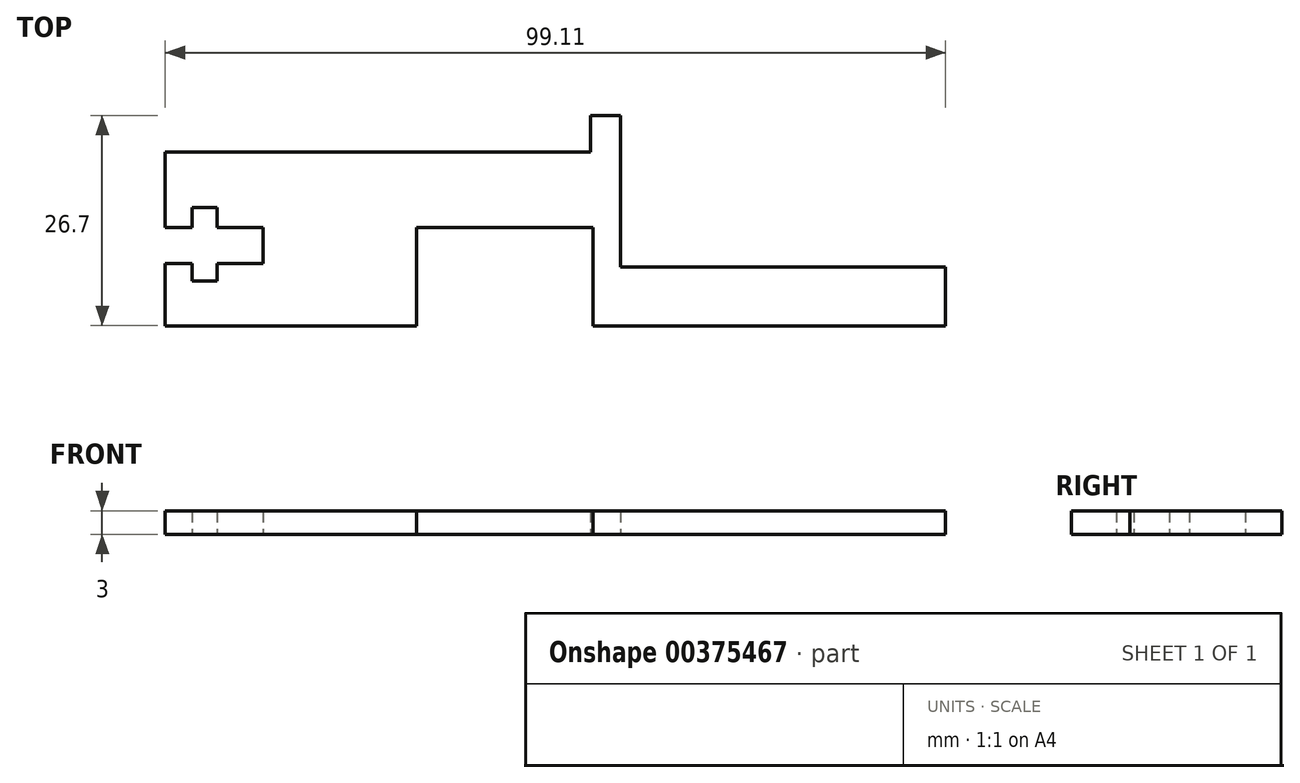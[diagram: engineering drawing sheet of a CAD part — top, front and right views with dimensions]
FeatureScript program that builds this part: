
annotation { "Feature Type Name" : "Feature", "Feature Type Description" : "" }
export const myFeature = defineFeature(function(context is Context, id is Id, definition is map)
    precondition{}
    {
        {
            var Q0;
            Q0=qCreatedBy(makeId("Top.planeOp"),FACE);
            var sketch = newSketch(context, id + "F0", { "sketchPlane" : qUnion([Q0])});
            skLineSegment(sketch, "E0", {"start": v(36.97, 9.66) * mm, "end": v(-7.78, 9.66) * mm});
            skLineSegment(sketch, "E1", {"start": v(-7.78, 9.66) * mm, "end": v(-7.78, 22.12) * mm});
            skLineSegment(sketch, "E2", {"start": v(-7.78, 22.12) * mm, "end": v(-30.25, 22.12) * mm});
            skLineSegment(sketch, "E3", {"start": v(-30.25, 22.12) * mm, "end": v(-30.25, 9.66) * mm});
            skLineSegment(sketch, "E4", {"start": v(-30.25, 9.66) * mm, "end": v(-62.14, 9.66) * mm});
            skLineSegment(sketch, "E5", {"start": v(-62.14, 9.66) * mm, "end": v(-62.14, 17.6) * mm});
            skLineSegment(sketch, "E6", {"start": v(-62.14, 17.6) * mm, "end": v(-58.76, 17.6) * mm});
            skLineSegment(sketch, "E7", {"start": v(-58.76, 17.6) * mm, "end": v(-58.76, 15.36) * mm});
            skLineSegment(sketch, "E8", {"start": v(-58.76, 15.36) * mm, "end": v(-55.57, 15.36) * mm});
            skLineSegment(sketch, "E9", {"start": v(-55.57, 15.36) * mm, "end": v(-55.57, 17.6) * mm});
            skLineSegment(sketch, "E10", {"start": v(-55.57, 17.6) * mm, "end": v(-49.72, 17.6) * mm});
            skLineSegment(sketch, "E11", {"start": v(-49.72, 17.6) * mm, "end": v(-49.72, 22.12) * mm});
            skLineSegment(sketch, "E12", {"start": v(-49.72, 22.12) * mm, "end": v(-55.57, 22.12) * mm});
            skLineSegment(sketch, "E13", {"start": v(-55.57, 22.12) * mm, "end": v(-55.57, 24.66) * mm});
            skLineSegment(sketch, "E14", {"start": v(-55.57, 24.66) * mm, "end": v(-58.76, 24.66) * mm});
            skLineSegment(sketch, "E15", {"start": v(-58.76, 24.66) * mm, "end": v(-58.76, 22.12) * mm});
            skLineSegment(sketch, "E16", {"start": v(-58.76, 22.12) * mm, "end": v(-62.14, 22.12) * mm});
            skLineSegment(sketch, "E17", {"start": v(-62.14, 22.12) * mm, "end": v(-62.14, 31.73) * mm});
            skLineSegment(sketch, "E18", {"start": v(-62.14, 31.73) * mm, "end": v(-8.13, 31.73) * mm});
            skLineSegment(sketch, "E19", {"start": v(-8.13, 31.73) * mm, "end": v(-8.13, 36.36) * mm});
            skLineSegment(sketch, "E20", {"start": v(-8.13, 36.36) * mm, "end": v(-4.31, 36.36) * mm});
            skLineSegment(sketch, "E21", {"start": v(-4.31, 36.36) * mm, "end": v(-4.31, 17.1) * mm});
            skLineSegment(sketch, "E22", {"start": v(-4.31, 17.1) * mm, "end": v(36.97, 17.1) * mm});
            skLineSegment(sketch, "E23", {"start": v(36.97, 17.1) * mm, "end": v(36.97, 9.66) * mm});
            skSolve(sketch);
        }
        {
            var Q0;
            Q0 = qSketchRegion(id + "F0", true);
            extrude(context, id + "F1", {"entities" : qUnion([Q0]), "depth" : 3 * mm});
        }
    });
